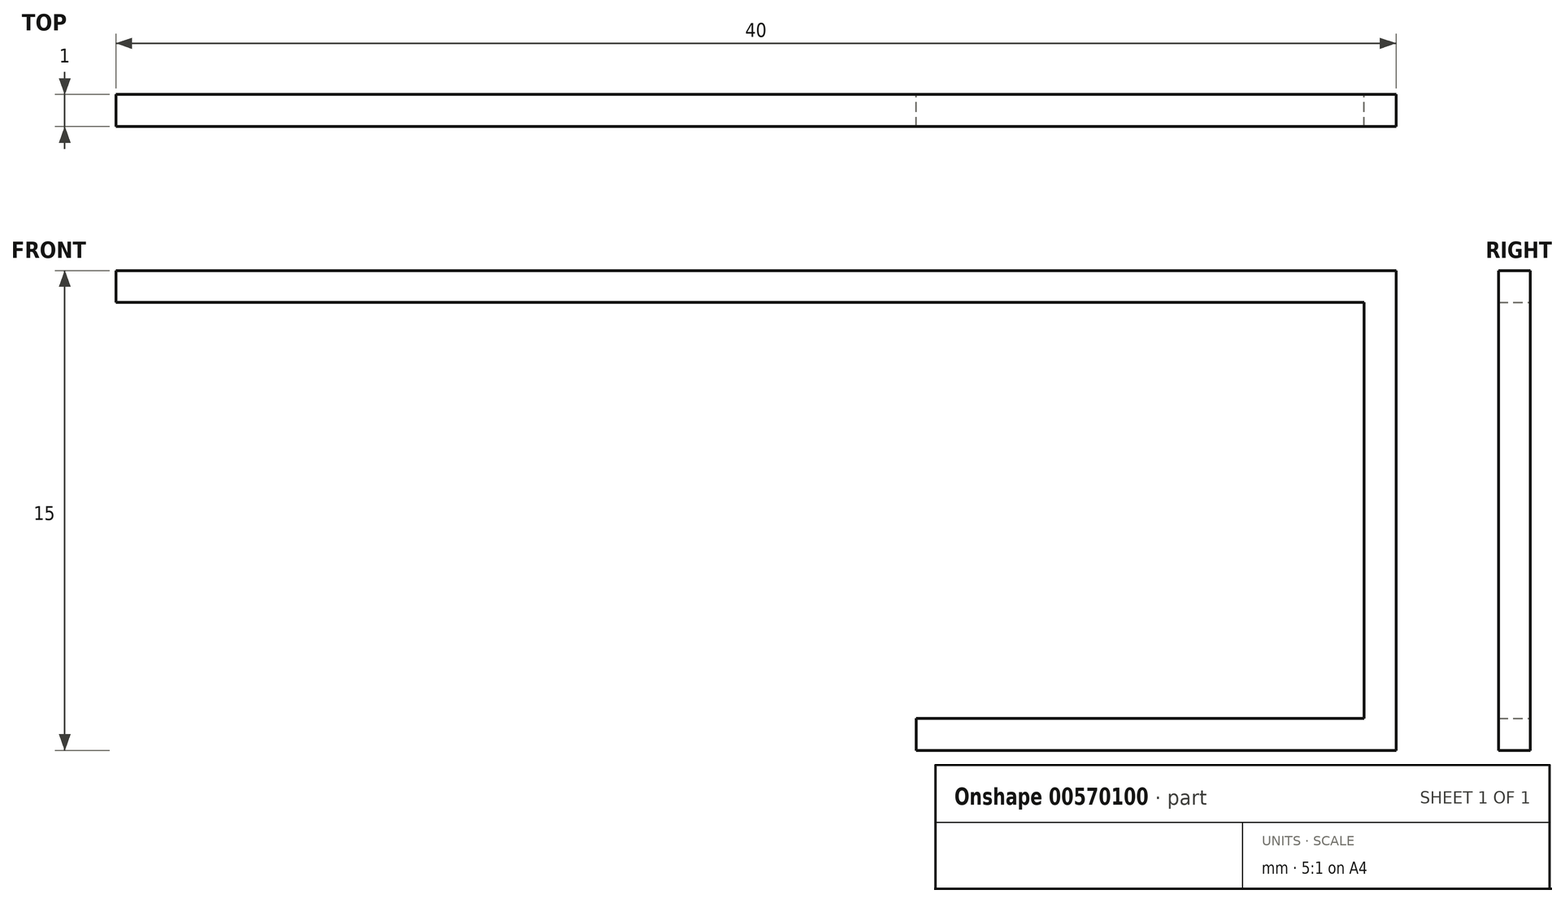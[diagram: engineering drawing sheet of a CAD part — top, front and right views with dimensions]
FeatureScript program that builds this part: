
annotation { "Feature Type Name" : "Feature", "Feature Type Description" : "" }
export const myFeature = defineFeature(function(context is Context, id is Id, definition is map)
    precondition{}
    {
        {
            var Q0;
            Q0=qCreatedBy(makeId("Front.planeOp"),FACE);
            var sketch = newSketch(context, id + "F0", { "sketchPlane" : qUnion([Q0])});
            skLineSegment(sketch, "E0.bottom", {"start": v(0, 0) * mm, "end": v(40, 0) * mm, "construction": true});
            skLineSegment(sketch, "E0.top", {"start": v(0, -15) * mm, "end": v(40, -15) * mm, "construction": true});
            skLineSegment(sketch, "E0.left", {"start": v(0, 0) * mm, "end": v(0, -15) * mm, "construction": true});
            skLineSegment(sketch, "E0.right", {"start": v(40, 0) * mm, "end": v(40, -15) * mm, "construction": true});
            skLineSegment(sketch, "E1", {"start": v(25, -15) * mm, "end": v(40, -15) * mm});
            skLineSegment(sketch, "E2", {"start": v(40, 0) * mm, "end": v(0, 0) * mm});
            skLineSegment(sketch, "E3", {"start": v(40, -15) * mm, "end": v(40, 0) * mm});
            skLineSegment(sketch, "E4.0", {"start": v(39, -1) * mm, "end": v(0, -1) * mm});
            skLineSegment(sketch, "E4.1", {"start": v(39, -14) * mm, "end": v(39, -1) * mm});
            skLineSegment(sketch, "E4.2", {"start": v(25, -14) * mm, "end": v(39, -14) * mm});
            skLineSegment(sketch, "E5", {"start": v(0, -1) * mm, "end": v(0, 0) * mm});
            skLineSegment(sketch, "E6", {"start": v(25, -15) * mm, "end": v(25, -14) * mm});
            skSolve(sketch);
        }
        {
            var Q0;
            Q0=makeQuery(id+"F0.imprint","IMPRINT",FACE,{"disambiguationData":[TD([[makeQuery(id+"F0.imprint","IMPRINT",EDGE,{"derivedFrom":sQuery(id+"F0.wireOp",EDGE,"E1")}),1.0]])]});
            extrude(context, id + "F1", {"entities" : qUnion([Q0]), "depth" : 1 * mm, "offsetDistance" : 25 * mm});
        }
    });
